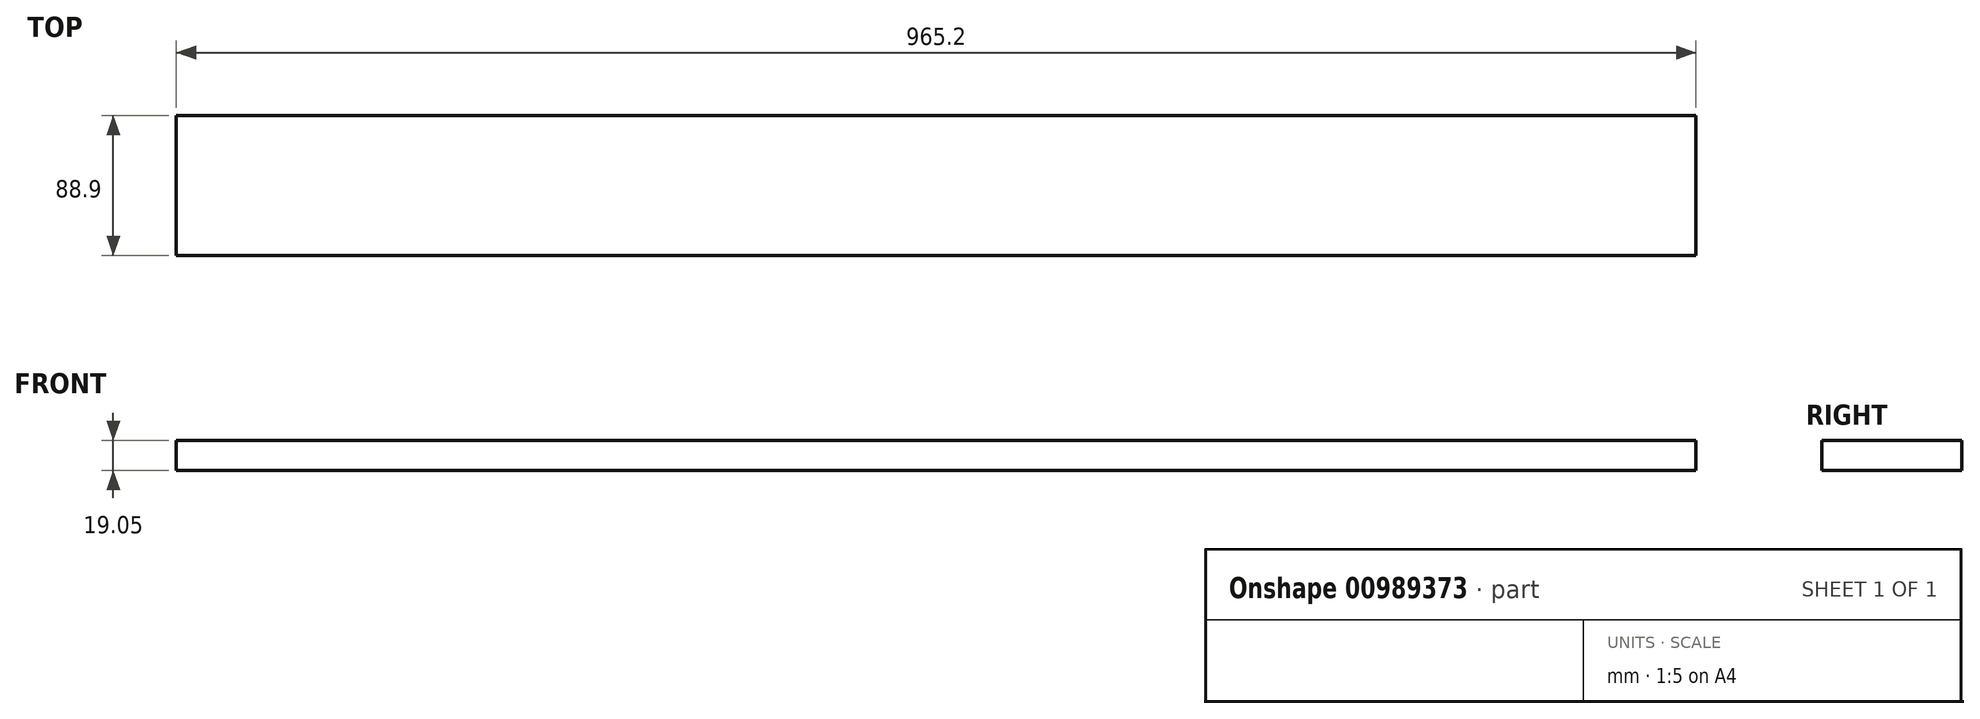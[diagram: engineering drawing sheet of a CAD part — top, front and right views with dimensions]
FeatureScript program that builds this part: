
annotation { "Feature Type Name" : "Feature", "Feature Type Description" : "" }
export const myFeature = defineFeature(function(context is Context, id is Id, definition is map)
    precondition{}
    {
        {
            var Q0;
            Q0=qCreatedBy(makeId("Right.planeOp"),FACE);
            var sketch = newSketch(context, id + "F0", { "sketchPlane" : qUnion([Q0])});
            skLineSegment(sketch, "E0.bottom", {"start": v(-63.5, 13.63) * mm, "end": v(25.4, 13.63) * mm});
            skLineSegment(sketch, "E0.top", {"start": v(-63.5, -5.42) * mm, "end": v(25.4, -5.42) * mm});
            skLineSegment(sketch, "E0.left", {"start": v(-63.5, 13.63) * mm, "end": v(-63.5, -5.42) * mm});
            skLineSegment(sketch, "E0.right", {"start": v(25.4, 13.63) * mm, "end": v(25.4, -5.42) * mm});
            skSolve(sketch);
        }
        {
            var Q0;
            Q0=makeQuery(id+"F0.imprint","IMPRINT",FACE,{"disambiguationData":[TD([[makeQuery(id+"F0.imprint","IMPRINT",EDGE,{"derivedFrom":sQuery(id+"F0.wireOp",EDGE,"E0.bottom")}),-1.0]])]});
            extrude(context, id + "F1", {"entities" : qUnion([Q0]), "depth" : 965.2 * mm, "offsetDistance" : 25.4 * mm});
        }
    });
